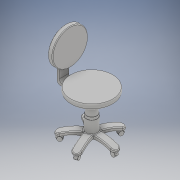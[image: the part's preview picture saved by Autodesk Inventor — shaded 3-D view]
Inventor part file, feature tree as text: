
AUTODESK INVENTOR PART (.ipt)
format: ipt  version: 2017 (Build 210142000, 142)  size: 729,600 bytes
history: native  units: in
note: dims shown in document units (in); Inventor stores cm internally (conversion verified against a paired STEP export)
features: sketch x17, extrude x14, fillet x8, other x4, plane x1, mirror x1, pattern_circular x1
ambient origin geometry x8: Origin, YZ Plane, XZ Plane, XY Plane, X Axis, Y Axis, Z Axis, Center Point
bodies: Solid1 (feature_tree)
feature tree (46):
  extrude  "seat"  Depth=1.1875in
  fillet  "curve bottom of seat"  Radius=0.625in
  fillet  "curv top of seat"  Radius=0.3in
  extrude  "solenoid connection to seat"  [1 undecoded]
  fillet  "curve solenoid connection to seat"  Radius=4.5in
  sketch  "Sketch3"  dims[d10=5.5in d11=0.0in d12=0.5in]
  plane  "Work Plane1"
  extrude  "solnoid connection to back rest horizantal"  Depth=0.5in
  extrude  "solnoid connection to back rest vertical"  Depth=1.417in
  fillet  "curve back rest connection outer"  Radius=0.25in
  fillet  "curve back rest connection inner"  Radius=0.1in
  sketch  "Sketch6"  dims[d22=0.246in d23=0.406in d24=1.6845in]
  extrude  "connection to back rest extextion"  Depth=0.1in
  fillet  "curve connection to back rest extextion"  Radius=0.342in
  extrude  "back rest"  Depth=0.406in
  fillet  "smooth back rest"  Radius=1.6845in
  other  "solnoid"
  extrude  "foot of chair"  Depth=0.3867in
  extrude  "curve added to foot"  Depth=1.7843in
  extrude  "smooth out the end of the foot"  Depth=1.161in
  extrude  "wheel connection to foot"  Depth=1.0in TaperAngle=0.0deg
  extrude  "wheel case"  Depth=0.6667in
  extrude  "wheel protection make"  Depth=3.0in TaperAngle=0.0deg
  extrude  "wheel protection cut"  Depth=0.0927in TaperAngle=0.0deg
  extrude  "wheel"  Depth=0.3438in TaperAngle=0.0deg
  other  "wheel curve face workplane"
  other  "wheel for foot"
  mirror  "Mirror the components for the wheel"
  pattern_circular  "Circular Pattern5"  [2 undecoded]
  fillet  "Fillet9"  Radius=0.1585in
  sketch  "Sketch1"  dims[d0=1.2in d1=0.0in d2=1.1875in d3=0.625in d4=0.3in d5=0.0in]
  sketch  "Sketch2"  dims[d6=0.5in d7=-0.5in d8=4.5in d9=0.0in]
  sketch  "Sketch4"  dims[d13=0.5in d14=1.417in d15=0.25in d16=0.0in d17=0.1in]
  sketch  "Sketch5"  dims[d18=0.7in d19=0.0in d20=0.1in d21=0.342in]
  sketch  "Sketch8"  dims[d25=0.0417in d26=0.3867in]
  sketch  "Sketch9"  dims[d27=0.0417in d28=1.7843in]
  sketch  "Sketch10"  dims[d29=90.0deg d34=1.161in]
  sketch  "Sketch11"  dims[d35=3.1875in d36=1.0in d37=0.0in]
  sketch  "Sketch12"  dims[d38=0.3333in d39=0.6667in]
  sketch  "Sketch13"  dims[d40=0.6667in d41=3.0in d42=0.0in]
  sketch  "Sketch15"  dims[d43=0.1955in d44=0.0927in d45=0.0in]
  sketch  "Sketch16"  dims[d46=0.4947in d47=0.3438in d48=0.0in]
  sketch  "Sketch17"  dims[d50=0.3855in]
  other  "Work Axis1"
  sketch  "Sketch19"  dims[d52=0.7247in]
  sketch  "Sketch21"  dims[d53=0.5in d54=0.0in d55=0.7057in d56=0.1585in d57=0.0in d58=0.648in d59=0.2283in d60=0.0in d63=90.0deg d71=0.2095in d72=0.0in d83=1.9685in d84=360.0deg d86=0.125in]
note: 3 required parameter values undecoded (feature->parameter linkage not recoverable at this tier; creation-order binding heuristic only, values carry confidence <= 0.55)
